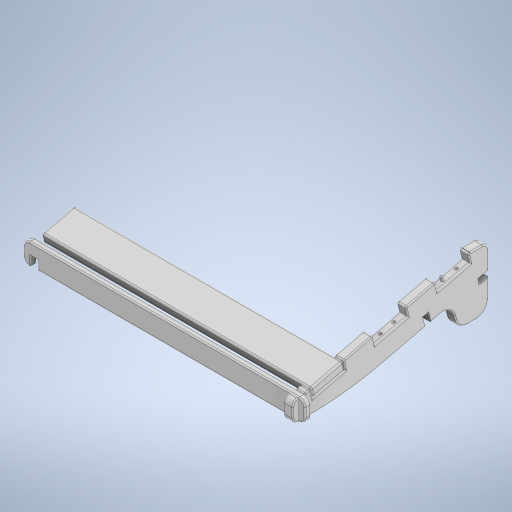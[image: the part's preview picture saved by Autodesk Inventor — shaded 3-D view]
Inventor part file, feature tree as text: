
AUTODESK INVENTOR PART (.ipt)
format: ipt  version: 2023 (Build 270158030, 158C)  size: 686,592 bytes
history: native  units: mm
features: fillet x17, extrude x11, sketch x10, other x4
ambient origin geometry x8: Origin, YZ Plane, XZ Plane, XY Plane, X Axis, Y Axis, Z Axis, Center Point
bodies: Body1 (feature_tree), Body2 (feature_tree), Body3 (feature_tree), Body4 (feature_tree)
feature tree (42):
  other  "Side_A"
  extrude  "Extrusion1"  Depth=320.0mm
  extrude  "Extrusion2"  Depth=15.0mm TaperAngle=0.0deg
  extrude  "Extrusion3"  Depth=55.0mm
  extrude  "Extrusion4"  Depth=50.0mm
  extrude  "Extrusion5"  Depth=15.0mm
  extrude  "Extrusion6"  Depth=15.0mm
  extrude  "Extrusion7"  Depth=15.0mm
  extrude  "Extrusion8"  Depth=10.0mm
  fillet  "Fillet1"  Radius=15.0mm
  fillet  "Fillet2"  Radius=440.0mm
  fillet  "Fillet3"  Radius=15.0mm
  fillet  "Fillet4"  Radius=17.0mm
  fillet  "Fillet5"  Radius=10.0mm
  fillet  "Fillet6"  Radius=15.0mm
  fillet  "Fillet7"  Radius=15.0mm
  fillet  "Fillet8"  Radius=10.0mm
  fillet  "Fillet9"  Radius=10.0mm
  fillet  "Fillet10"  Radius=18.0mm
  fillet  "Fillet11"  Radius=10.0mm
  fillet  "Fillet12"  Radius=17.0mm
  fillet  "Fillet13"  Radius=35.0mm
  fillet  "Fillet14"  Radius=10.0mm
  fillet  "Fillet15"  Radius=20.0mm
  extrude  "Extrusion9"  Depth=10.0mm
  fillet  "Fillet16"  Radius=10.0mm
  extrude  "Extrusion10"  Depth=1.3mm
  extrude  "Extrusion11"  Depth=10.0mm
  fillet  "Fillet17"  Radius=18.0mm
  sketch  "Sketch2"  dims[d0=100.0mm d1=320.0mm]
  sketch  "Sketch3"  dims[d3=30.0mm d4=15.0mm d5=0.0mm]
  sketch  "Sketch4"  dims[d6=55.0mm d7=55.0mm]
  other  "CrossBar1"
  sketch  "Sketch5"  dims[d8=55.0mm d9=50.0mm]
  sketch  "Sketch6"  dims[d10=50.0mm d12=15.0mm]
  other  "End Foot"
  sketch  "Sketch7"  dims[d13=15.0mm d14=15.0mm]
  sketch  "Sketch8"  dims[d15=15.0mm d16=0.0mm d17=35.0mm]
  sketch  "Sketch9"  dims[d18=50.0mm d19=59.956952mm d20=15.0mm d21=0.0mm d22=440.0mm d23=15.0mm d24=0.0mm d25=17.0mm d26=10.0mm d28=15.0mm d29=0.0mm d33=15.0mm d34=10.0mm d35=10.0mm d36=0.0mm d37=18.0mm d38=10.0mm d39=17.0mm d40=35.0mm d41=10.0mm d42=0.0mm d46=20.0mm]
  sketch  "Sketch10"  dims[d49=35.0mm d50=29.12457mm d51=10.0mm]
  sketch  "Sketch11"  dims[d52=10.0mm d53=30.0mm d54=10.0mm d55=18.0mm d56=15.0mm d57=0.0mm d58=500.0mm d59=20.0mm d60=20.0mm d61=10.0mm d62=10.0mm d63=10.0mm d64=3.0mm d65=3.0mm d66=3.0mm d67=2.0mm d68=2.0mm d69=2.0mm d70=2.0mm d71=2.0mm d72=3.0mm d73=5.0mm d74=16.0mm d75=16.0mm d76=7.5mm d77=7.5mm d78=15.0mm d79=0.0mm d80=16.0mm d81=16.0mm d82=16.0mm d83=16.0mm d84=3.0mm d85=7.5mm d86=7.5mm d87=7.5mm d88=0.0mm d89=15.0mm d90=0.0mm d91=1.3mm]
  other  "5mm Dowl"
